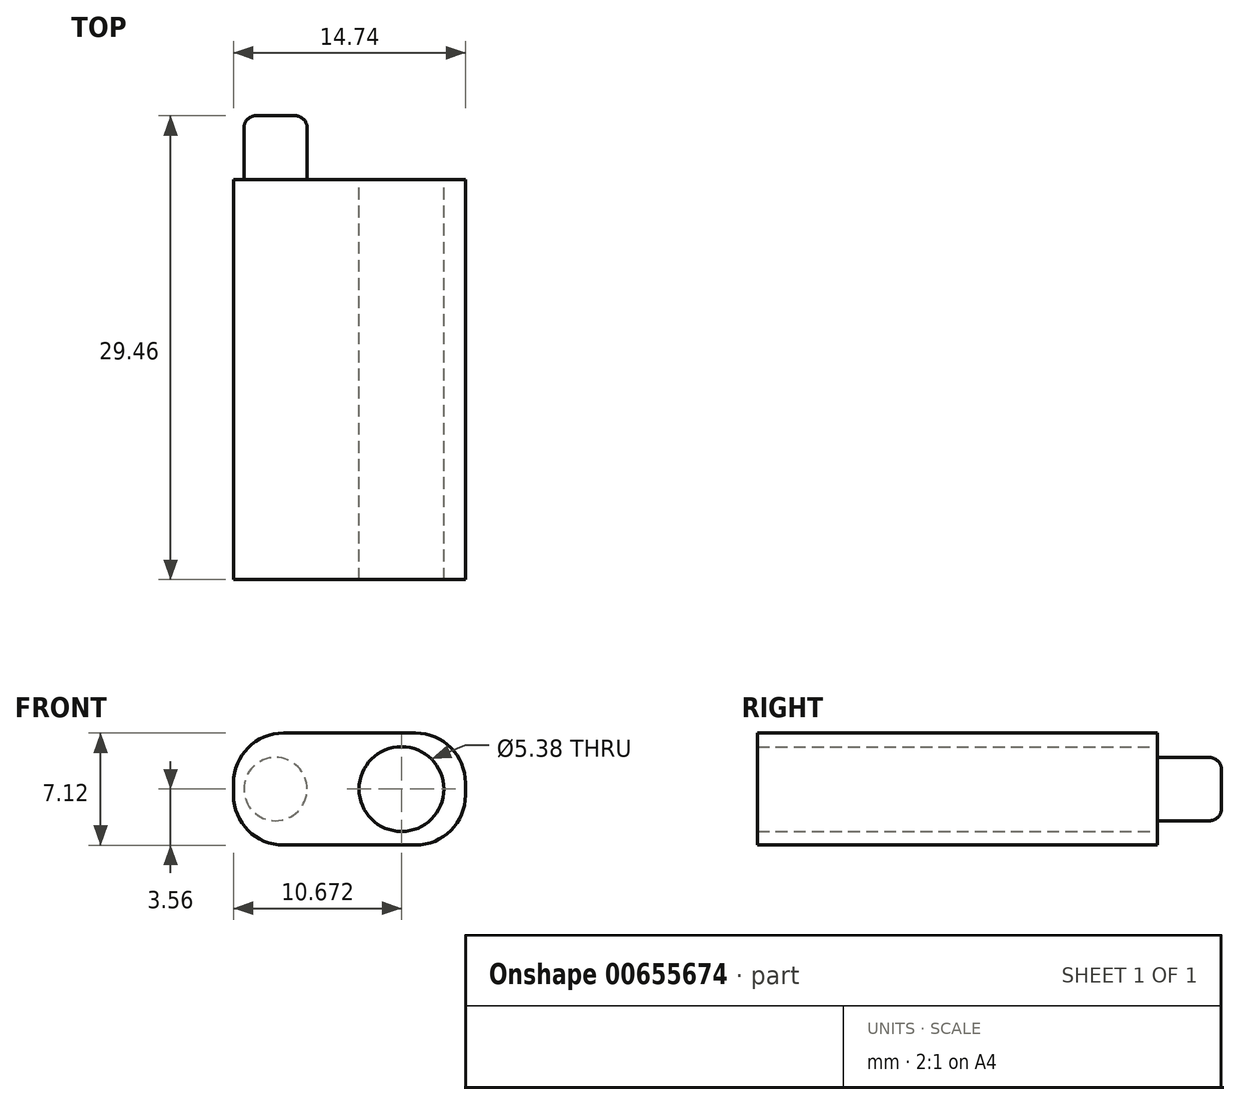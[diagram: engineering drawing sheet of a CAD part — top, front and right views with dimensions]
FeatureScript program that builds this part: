
annotation { "Feature Type Name" : "Feature", "Feature Type Description" : "" }
export const myFeature = defineFeature(function(context is Context, id is Id, definition is map)
    precondition{}
    {
        {
            var Q0;
            Q0=qCreatedBy(makeId("Front.planeOp"),FACE);
            var sketch = newSketch(context, id + "F0", { "sketchPlane" : qUnion([Q0])});
            skLineSegment(sketch, "E0.bottom", {"start": v(7.37, 3.56) * mm, "end": v(-7.37, 3.56) * mm});
            skLineSegment(sketch, "E0.top", {"start": v(7.37, -3.56) * mm, "end": v(-7.37, -3.56) * mm});
            skLineSegment(sketch, "E0.left", {"start": v(7.37, 3.56) * mm, "end": v(7.37, -3.56) * mm});
            skLineSegment(sketch, "E0.right", {"start": v(-7.37, 3.56) * mm, "end": v(-7.37, -3.56) * mm});
            skPoint(sketch, "E0.middle", {"position": v(0, 0) * mm});
            skCircle(sketch, "E1", {"center": v(3.3, 0) * mm, "radius": 2.7 * mm});
            skCircle(sketch, "E2", {"center": v(-4.7, 0) * mm, "radius": 2 * mm});
            skSolve(sketch);
        }
        {
            var Q0;
            Q0=makeQuery(id+"F0.imprint","IMPRINT",FACE,{"disambiguationData":[TD([[makeQuery(id+"F0.imprint","IMPRINT",EDGE,{"derivedFrom":sQuery(id+"F0.wireOp",EDGE,"E0.bottom")}),1.0]])]});
            var Q1;
            Q1=makeQuery(id+"F0.imprint","IMPRINT",FACE,{"disambiguationData":[TD([[makeQuery(id+"F0.imprint","IMPRINT",EDGE,{"derivedFrom":sQuery(id+"F0.wireOp",EDGE,"E1")}),1.0]])]});
            var Q2;
            Q2=makeQuery(id+"F0.imprint","IMPRINT",FACE,{"disambiguationData":[TD([[makeQuery(id+"F0.imprint","IMPRINT",EDGE,{"derivedFrom":sQuery(id+"F0.wireOp",EDGE,"E2")}),1.0]])]});
            var Q3;
            Q3=makeQuery(id+"F0.imprint","IMPRINT",FACE,{"disambiguationData":[TD([[makeQuery(id+"F0.imprint","IMPRINT",EDGE,{"derivedFrom":sQuery(id+"F0.wireOp",EDGE,"85gi6sC0-igKE-fCZt-ul8r-zRTyUoMfWGpD")}),1.0]])]});
            extrude(context, id + "F1", {"entities" : qUnion([Q0, Q1, Q2, Q3]), "depth" : 25.4 * mm, "offsetDistance" : 25.4 * mm});
        }
        {
            var Q0;
            Q0=makeQuery(id+"F0.imprint","IMPRINT",FACE,{"disambiguationData":[TD([[makeQuery(id+"F0.imprint","IMPRINT",EDGE,{"derivedFrom":sQuery(id+"F0.wireOp",EDGE,"E1")}),1.0]])]});
            extrude(context, id + "F2", {"entities" : qUnion([Q0]), "operationType" : NewBodyOperationType.REMOVE, "endBound" : BoundingType.THROUGH_ALL, "depth" : 1.02 * mm, "offsetDistance" : 25.4 * mm});
        }
        {
            var Q0;
            Q0=makeQuery(id+"F0.imprint","IMPRINT",FACE,{"disambiguationData":[TD([[makeQuery(id+"F0.imprint","IMPRINT",EDGE,{"derivedFrom":sQuery(id+"F0.wireOp",EDGE,"E2")}),1.0]])]});
            extrude(context, id + "F3", {"entities" : qUnion([Q0]), "operationType" : NewBodyOperationType.ADD, "oppositeDirection" : true, "depth" : 4.06 * mm, "offsetDistance" : 25.4 * mm});
        }
        {
            var Q0;
            Q0=makeQuery(id+"F0.imprint","IMPRINT",FACE,{"disambiguationData":[TD([[makeQuery(id+"F0.imprint","IMPRINT",EDGE,{"derivedFrom":sQuery(id+"F0.wireOp",EDGE,"E1")}),1.0]])]});
            var sketch = newSketch(context, id + "F4", { "sketchPlane" : qUnion([Q0])});
            skCircle(sketch, "E3", {"center": v(3.3, 0) * mm, "radius": 1.32 * mm});
            skSolve(sketch);
        }
        {
            var Q0;
            Q0 = qSketchRegion(id + "F4", true);
            extrude(context, id + "F5", {"entities" : qUnion([Q0]), "operationType" : NewBodyOperationType.REMOVE, "endBound" : BoundingType.THROUGH_ALL, "depth" : 25.4 * mm, "offsetDistance" : 25.4 * mm});
        }
        {
            var Q0;
            Q0=makeQuery(id+"F3.opExtrude","CAP_EDGE",EDGE,{"disambiguationData":[OSD([sQuery(id+"F0.wireOp",EDGE,"E2")])],"isStart":false});
            fillet(context, id + "F6", {"entities" : qUnion([Q0]), "radius" : 0.76 * mm, "tangentPropagation" : true, "allowEdgeOverflow" : false});
        }
        {
            var Q0;
            Q0=makeQuery(id+"F1.opExtrude","SWEPT_EDGE",EDGE,{"disambiguationData":[OSD([sQuery(id+"F0.wireOp",EDGE,"E0.bottom"),sQuery(id+"F0.wireOp",EDGE,"E0.left")])]});
            var Q1;
            Q1=makeQuery(id+"F1.opExtrude","SWEPT_EDGE",EDGE,{"disambiguationData":[OSD([sQuery(id+"F0.wireOp",EDGE,"E0.top"),sQuery(id+"F0.wireOp",EDGE,"E0.left")])]});
            var Q2;
            Q2=makeQuery(id+"F1.opExtrude","SWEPT_EDGE",EDGE,{"disambiguationData":[OSD([sQuery(id+"F0.wireOp",EDGE,"E0.top"),sQuery(id+"F0.wireOp",EDGE,"E0.right")])]});
            var Q3;
            Q3=makeQuery(id+"F1.opExtrude","SWEPT_EDGE",EDGE,{"disambiguationData":[OSD([sQuery(id+"F0.wireOp",EDGE,"E0.bottom"),sQuery(id+"F0.wireOp",EDGE,"E0.right")])]});
            fillet(context, id + "F7", {"entities" : qUnion([Q0, Q1, Q2, Q3]), "radius" : 3.17 * mm, "tangentPropagation" : true, "allowEdgeOverflow" : false});
        }
    });
